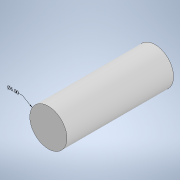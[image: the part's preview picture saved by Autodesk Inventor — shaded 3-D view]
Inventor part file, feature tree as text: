
AUTODESK INVENTOR PART (.ipt)
format: ipt  version: 2020.3 (Build 243373000, 373)  size: 96,256 bytes
history: native  units: in
note: dims shown in document units (in); Inventor stores cm internally (conversion verified against a paired STEP export)
features: other x2, extrude x1, sketch x1
ambient origin geometry x8: Origin, YZ Plane, XZ Plane, XY Plane, X Axis, Y Axis, Z Axis, Center Point
bodies: Solid1 (feature_tree)
feature tree (4):
  other  "Annotations"
  extrude  "Extrusion1"  Depth=1.032in
  sketch  "Sketch1"  dims[d2=0.0in d3=1.032in d4=6.0in]
  other  "Diameter Dimension 1"
